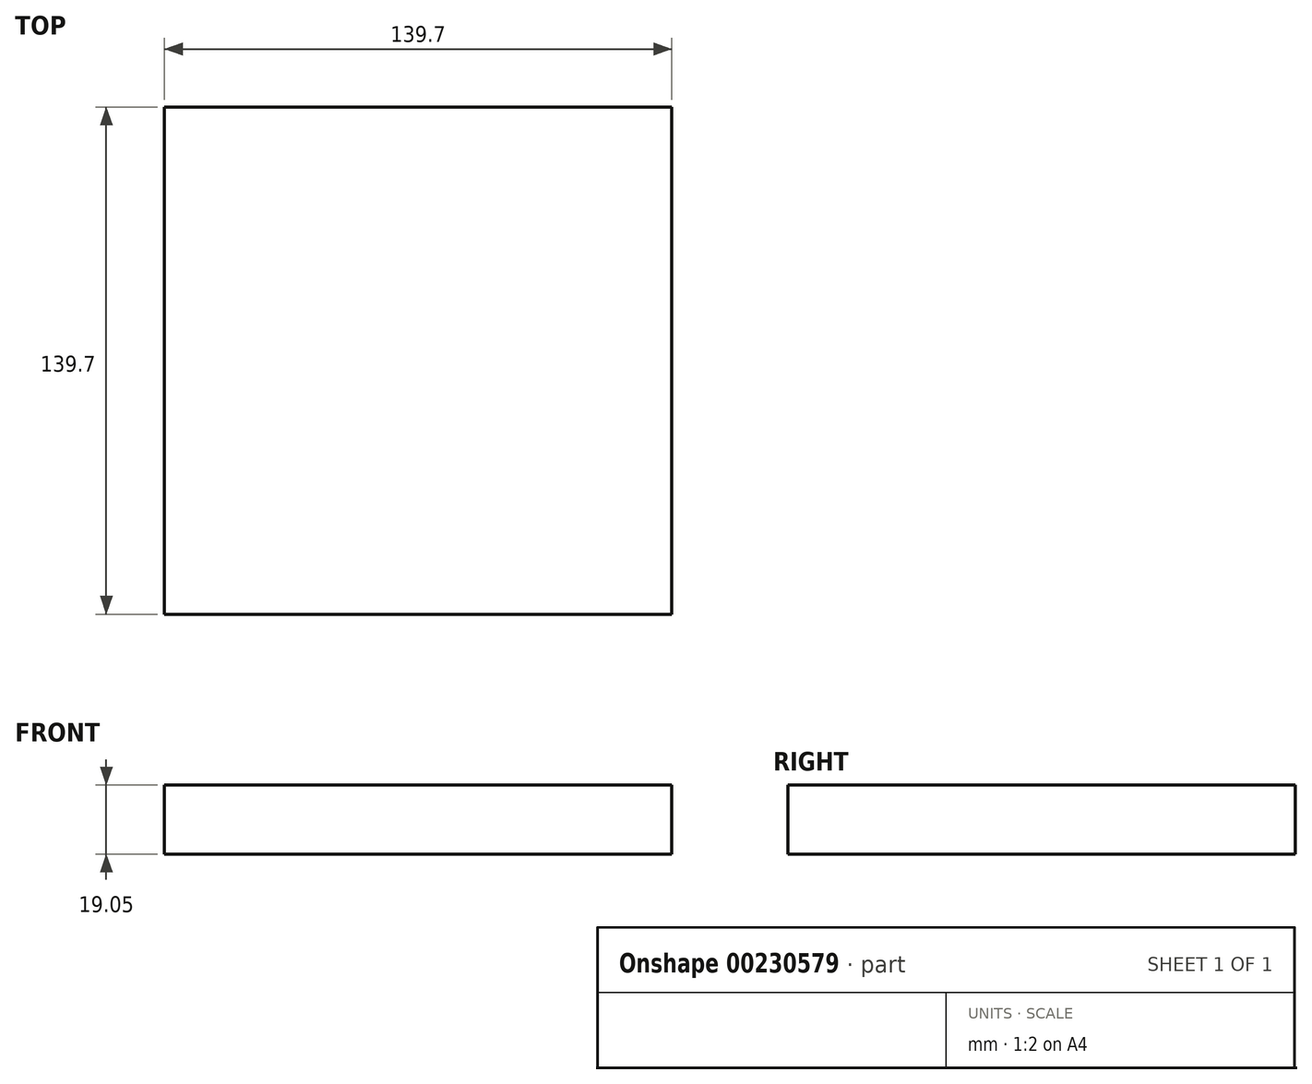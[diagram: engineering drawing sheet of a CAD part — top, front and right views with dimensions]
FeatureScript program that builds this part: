
annotation { "Feature Type Name" : "Feature", "Feature Type Description" : "" }
export const myFeature = defineFeature(function(context is Context, id is Id, definition is map)
    precondition{}
    {
        {
            var Q0;
            Q0=qCreatedBy(makeId("Top.planeOp"),FACE);
            var sketch = newSketch(context, id + "F0", { "sketchPlane" : qUnion([Q0])});
            skLineSegment(sketch, "E0.bottom", {"start": v(-69.85, -69.85) * mm, "end": v(69.85, -69.85) * mm});
            skLineSegment(sketch, "E0.top", {"start": v(-69.85, 69.85) * mm, "end": v(69.85, 69.85) * mm});
            skLineSegment(sketch, "E0.left", {"start": v(-69.85, -69.85) * mm, "end": v(-69.85, 69.85) * mm});
            skLineSegment(sketch, "E0.right", {"start": v(69.85, -69.85) * mm, "end": v(69.85, 69.85) * mm});
            skPoint(sketch, "E0.middle", {"position": v(0, 0) * mm});
            skSolve(sketch);
        }
        {
            var Q0;
            Q0 = qSketchRegion(id + "F0", true);
            extrude(context, id + "F1", {"entities" : qUnion([Q0]), "depth" : 19.05 * mm});
        }
    });
